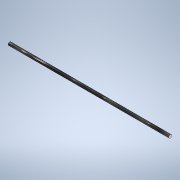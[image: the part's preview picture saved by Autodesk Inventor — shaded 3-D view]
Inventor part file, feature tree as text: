
AUTODESK INVENTOR PART (.ipt)
format: ipt  version: 2021 (Build 250183000, 183)  size: 101,888 bytes
history: native  units: in
note: dims shown in document units (in); Inventor stores cm internally (conversion verified against a paired STEP export)
features: extrude x1, sketch x1
ambient origin geometry x8: Origin, YZ Plane, XZ Plane, XY Plane, X Axis, Y Axis, Z Axis, Center Point
bodies: Solid1 (feature_tree)
feature tree (2):
  extrude  "Extrusion1"  Depth=0.2664in TaperAngle=0.0deg
  sketch  "Sketch1"  dims[d0=0.0053in d1=0.2664in d2=0.0in]
